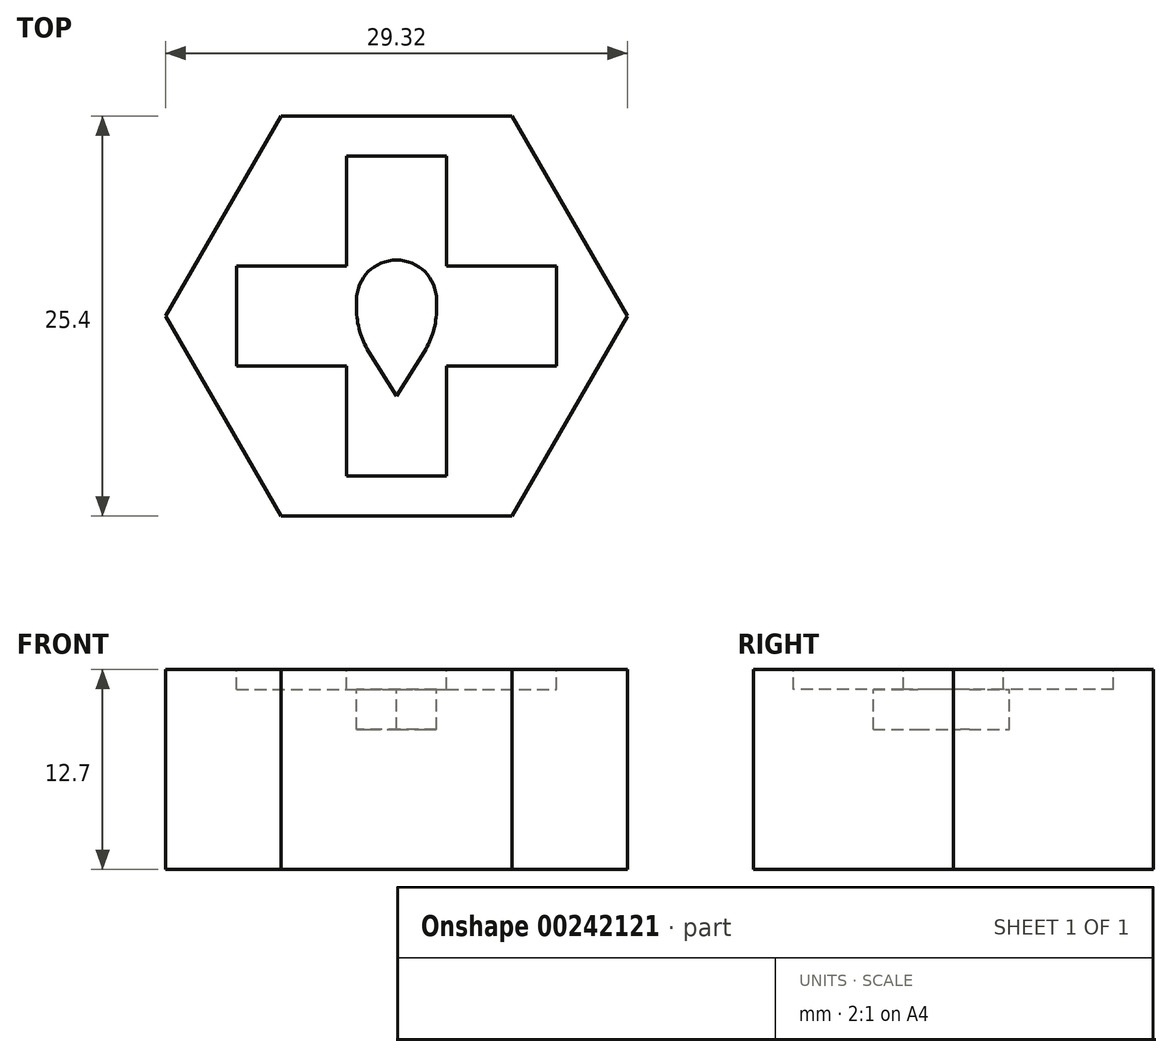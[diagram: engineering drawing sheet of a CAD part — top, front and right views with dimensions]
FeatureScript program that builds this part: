
annotation { "Feature Type Name" : "Feature", "Feature Type Description" : "" }
export const myFeature = defineFeature(function(context is Context, id is Id, definition is map)
    precondition{}
    {
        {
            var Q0;
            Q0=qCreatedBy(makeId("Top.planeOp"),FACE);
            var sketch = newSketch(context, id + "F0", { "sketchPlane" : qUnion([Q0])});
            skCircle(sketch, "E0.cCircle", {"center": v(0, 0) * mm, "radius": 12.7 * mm, "construction": true});
            skLineSegment(sketch, "E0.0", {"start": v(7.33, 12.7) * mm, "end": v(14.66, 0) * mm});
            skLineSegment(sketch, "E0.1", {"start": v(14.66, 0) * mm, "end": v(7.33, -12.7) * mm});
            skLineSegment(sketch, "E0.2", {"start": v(7.33, -12.7) * mm, "end": v(-7.33, -12.7) * mm});
            skLineSegment(sketch, "E0.3", {"start": v(-7.33, -12.7) * mm, "end": v(-14.66, 0) * mm});
            skLineSegment(sketch, "E0.4", {"start": v(-14.66, 0) * mm, "end": v(-7.33, 12.7) * mm});
            skLineSegment(sketch, "E0.5", {"start": v(-7.33, 12.7) * mm, "end": v(7.33, 12.7) * mm});
            skPoint(sketch, "E0.0.midPoint", {"position": v(11, 6.35) * mm});
            skSolve(sketch);
        }
        {
            var Q0;
            Q0 = qSketchRegion(id + "F0", true);
            extrude(context, id + "F1", {"entities" : qUnion([Q0]), "depth" : 12.7 * mm});
        }
        {
            var Q0;
            Q0=makeQuery(id+"F1.opExtrude","CAP_FACE",FACE,{"disambiguationData":[OSD([sQuery(id+"F0.wireOp",EDGE,"E0.0"),sQuery(id+"F0.wireOp",EDGE,"E0.1"),sQuery(id+"F0.wireOp",EDGE,"E0.2"),sQuery(id+"F0.wireOp",EDGE,"E0.3"),sQuery(id+"F0.wireOp",EDGE,"E0.4"),sQuery(id+"F0.wireOp",EDGE,"E0.5")])],"isStart":false});
            var sketch = newSketch(context, id + "F2", { "sketchPlane" : qUnion([Q0])});
            skLineSegment(sketch, "E1.bottom", {"start": v(-3.17, 10.16) * mm, "end": v(3.18, 10.16) * mm});
            skLineSegment(sketch, "E1.top", {"start": v(-3.17, -10.16) * mm, "end": v(3.18, -10.16) * mm});
            skLineSegment(sketch, "E1.left", {"start": v(-3.17, 10.16) * mm, "end": v(-3.17, 3.18) * mm});
            skLineSegment(sketch, "E1.right", {"start": v(3.18, 10.16) * mm, "end": v(3.18, 3.18) * mm});
            skLineSegment(sketch, "E2.bottom", {"start": v(-10.16, 3.17) * mm, "end": v(-3.17, 3.18) * mm});
            skLineSegment(sketch, "E2.top", {"start": v(-10.16, -3.18) * mm, "end": v(-3.17, -3.17) * mm});
            skLineSegment(sketch, "E2.left", {"start": v(-10.16, 3.17) * mm, "end": v(-10.16, -3.18) * mm});
            skLineSegment(sketch, "E2.right", {"start": v(10.16, 3.18) * mm, "end": v(10.16, -3.17) * mm});
            skLineSegment(sketch, "E3.trimOffspring", {"start": v(3.18, 3.18) * mm, "end": v(10.16, 3.18) * mm});
            skLineSegment(sketch, "E4.trimOffspring", {"start": v(3.18, -3.17) * mm, "end": v(3.18, -10.16) * mm});
            skLineSegment(sketch, "E5.trimOffspring", {"start": v(-3.17, -3.17) * mm, "end": v(-3.17, -10.16) * mm});
            skLineSegment(sketch, "E6.trimOffspring", {"start": v(3.18, -3.17) * mm, "end": v(10.16, -3.17) * mm});
            skSolve(sketch);
        }
        {
            var Q0;
            Q0 = qSketchRegion(id + "F2", true);
            extrude(context, id + "F3", {"entities" : qUnion([Q0]), "operationType" : NewBodyOperationType.REMOVE, "oppositeDirection" : true, "depth" : 1.27 * mm});
        }
        {
            var Q0;
            Q0=makeQuery(id+"F3.boolean.opBoolean","COPY",FACE,{"derivedFrom":makeQuery(id+"F3.opExtrude","CAP_FACE",FACE,{"disambiguationData":[OSD([sQuery(id+"F2.wireOp",EDGE,"E1.bottom"),sQuery(id+"F2.wireOp",EDGE,"E1.top"),sQuery(id+"F2.wireOp",EDGE,"E1.left"),sQuery(id+"F2.wireOp",EDGE,"E1.right"),sQuery(id+"F2.wireOp",EDGE,"E2.bottom"),sQuery(id+"F2.wireOp",EDGE,"E2.top"),sQuery(id+"F2.wireOp",EDGE,"E2.left"),sQuery(id+"F2.wireOp",EDGE,"E2.right"),sQuery(id+"F2.wireOp",EDGE,"E3.trimOffspring"),sQuery(id+"F2.wireOp",EDGE,"E4.trimOffspring"),sQuery(id+"F2.wireOp",EDGE,"E5.trimOffspring"),sQuery(id+"F2.wireOp",EDGE,"E6.trimOffspring")])],"isStart":false})});
            var sketch = newSketch(context, id + "F4", { "sketchPlane" : qUnion([Q0])});
            skArc(sketch, "E7", {"start": v(2.54, 1.02) * mm, "mid": v(0, 3.56) * mm, "end": v(-2.54, 1.02) * mm});
            skLineSegment(sketch, "E8", {"start": v(0, 1.02) * mm, "end": v(-2.54, 1.02) * mm, "construction": true});
            skLineSegment(sketch, "E9", {"start": v(0, 1.02) * mm, "end": v(2.54, 1.02) * mm, "construction": true});
            skLineSegment(sketch, "E10", {"start": v(2.54, 1.02) * mm, "end": v(2.54, 0.44) * mm});
            skLineSegment(sketch, "E11", {"start": v(-2.54, 1.02) * mm, "end": v(-2.54, 0.44) * mm});
            skLineSegment(sketch, "E12", {"start": v(-1.77, -2.25) * mm, "end": v(0, -5.08) * mm});
            skLineSegment(sketch, "E13", {"start": v(0, -5.08) * mm, "end": v(1.77, -2.25) * mm});
            skPoint(sketch, "E14.visualSharp", {"position": v(2.54, -1.02) * mm});
            skArc(sketch, "E14.filletArc", {"start": v(1.77, -2.25) * mm, "mid": v(2.34, -0.96) * mm, "end": v(2.54, 0.44) * mm});
            skPoint(sketch, "E15.visualSharp", {"position": v(-2.54, -1.02) * mm});
            skArc(sketch, "E15.filletArc", {"start": v(-2.54, 0.44) * mm, "mid": v(-2.34, -0.96) * mm, "end": v(-1.77, -2.25) * mm});
            skSolve(sketch);
        }
        {
            var Q0;
            Q0 = qSketchRegion(id + "F4", true);
            extrude(context, id + "F5", {"entities" : qUnion([Q0]), "operationType" : NewBodyOperationType.REMOVE, "oppositeDirection" : true, "depth" : 2.54 * mm});
        }
    });
